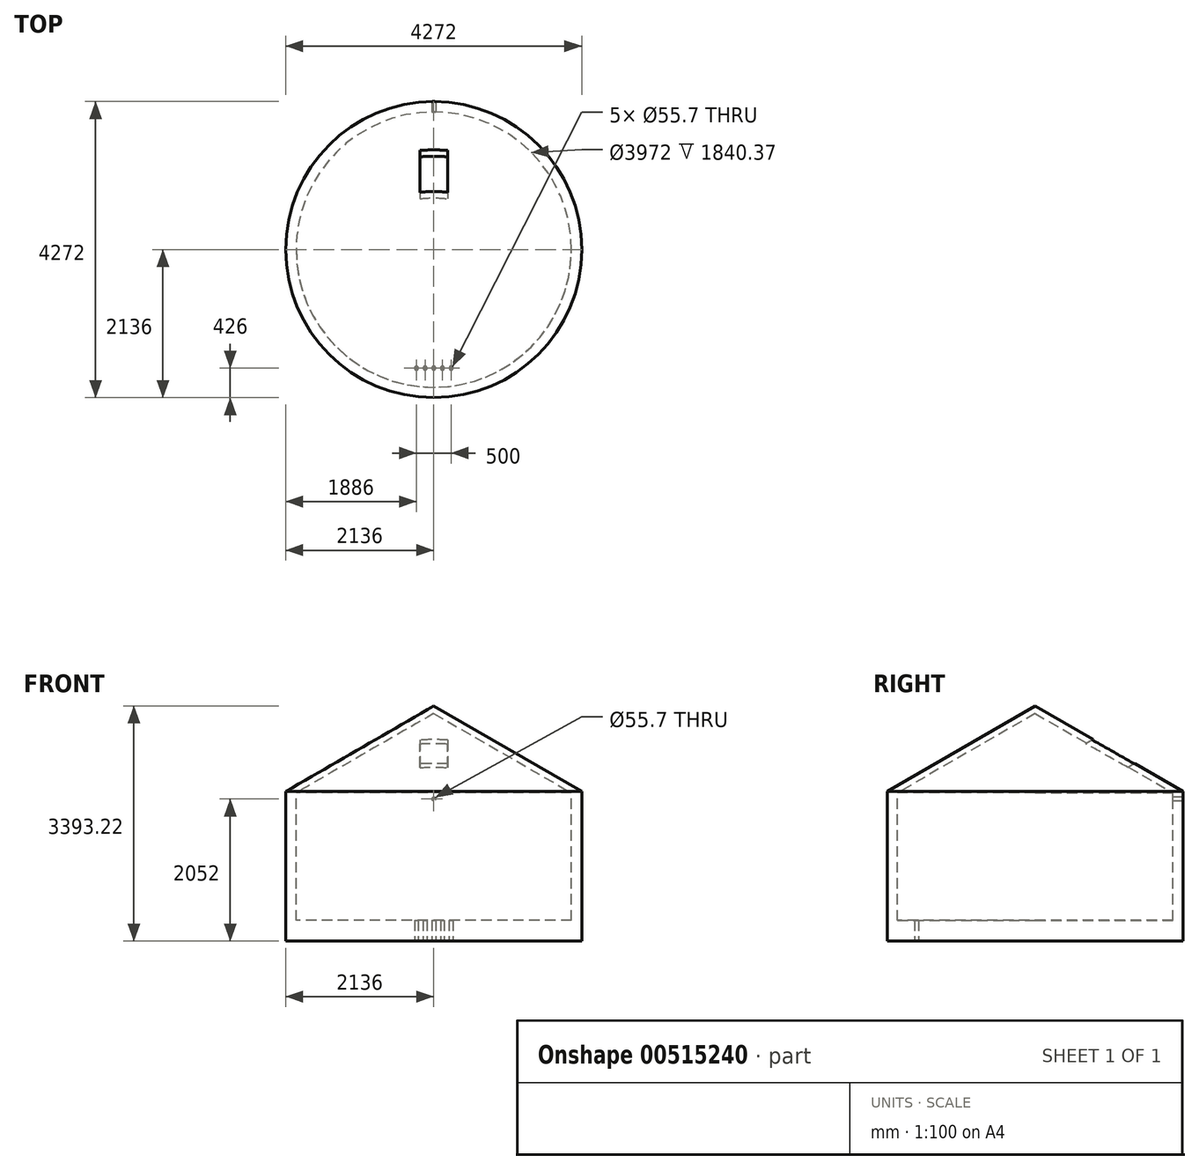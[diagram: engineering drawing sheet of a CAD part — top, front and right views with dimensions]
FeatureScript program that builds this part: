
annotation { "Feature Type Name" : "Feature", "Feature Type Description" : "" }
export const myFeature = defineFeature(function(context is Context, id is Id, definition is map)
    precondition{}
    {
        {
            var Q0;
            Q0=qCreatedBy(makeId("Front.planeOp"),FACE);
            var sketch = newSketch(context, id + "F0", { "sketchPlane" : qUnion([Q0])});
            skLineSegment(sketch, "E0", {"start": v(0, 0) * mm, "end": v(2136, 0) * mm});
            skLineSegment(sketch, "E1", {"start": v(2136, 0) * mm, "end": v(2136, 2160) * mm});
            skLineSegment(sketch, "E2", {"start": v(2136, 2160) * mm, "end": v(0, 3393.22) * mm});
            skLineSegment(sketch, "E3", {"start": v(0, 3393.22) * mm, "end": v(0, 3286.99) * mm});
            skLineSegment(sketch, "E4", {"start": v(0, 3286.99) * mm, "end": v(1986, 2140.37) * mm});
            skLineSegment(sketch, "E5", {"start": v(1986, 2140.37) * mm, "end": v(1986, 300) * mm});
            skLineSegment(sketch, "E6", {"start": v(1986, 300) * mm, "end": v(0, 300) * mm});
            skLineSegment(sketch, "E7", {"start": v(0, 300) * mm, "end": v(0, 0) * mm});
            skSolve(sketch);
        }
        {
            var Q0;
            Q0=sQuery(id+"F0.wireOp",EDGE,"E0");
            cPlane(context, id + "F1", {"entities" : qUnion([Q0]), "cplaneType" : CPlaneType.LINE_ANGLE, "offset" : 25 * mm, "angle" : 30 * degree, "width" : 150 * mm, "height" : 150 * mm});
        }
        {
            var Q0;
            Q0=qCreatedBy(id+"F1.planeOp",FACE);
            var sketch = newSketch(context, id + "F2", { "sketchPlane" : qUnion([Q0])});
            skLineSegment(sketch, "E8.bottom", {"start": v(-200, 2100) * mm, "end": v(200, 2100) * mm});
            skLineSegment(sketch, "E8.top", {"start": v(-200, 1500) * mm, "end": v(200, 1500) * mm});
            skLineSegment(sketch, "E8.left", {"start": v(-200, 2100) * mm, "end": v(-200, 1500) * mm});
            skLineSegment(sketch, "E9.MirrorCS", {"start": v(200, 2100) * mm, "end": v(200, 1500) * mm});
            skSolve(sketch);
        }
        {
            var Q0;
            Q0=qCreatedBy(makeId("Top.planeOp"),FACE);
            var sketch = newSketch(context, id + "F3", { "sketchPlane" : qUnion([Q0])});
            skLineSegment(sketch, "E10", {"start": v(282.73, -1710) * mm, "end": v(-1173.43, -1710) * mm, "construction": true});
            skCircle(sketch, "E11", {"center": v(125, -1710) * mm, "radius": 27.85 * mm});
            skCircle(sketch, "E12", {"center": v(-250, -1710) * mm, "radius": 27.85 * mm});
            skCircle(sketch, "E13", {"center": v(-125, -1710) * mm, "radius": 27.85 * mm});
            skCircle(sketch, "E14", {"center": v(0, -1710) * mm, "radius": 27.85 * mm});
            skCircle(sketch, "E15", {"center": v(250, -1710) * mm, "radius": 27.85 * mm});
            skSolve(sketch);
        }
        {
            var Q0;
            Q0=makeQuery(id+"F0.imprint","IMPRINT",FACE,{"disambiguationData":[TD([[makeQuery(id+"F0.imprint","IMPRINT",EDGE,{"derivedFrom":sQuery(id+"F0.wireOp",EDGE,"E0")}),1.0]])]});
            var Q1;
            Q1=sQuery(id+"F0.wireOp",EDGE,"E7");
            revolve(context, id + "F4", {"entities" : qUnion([Q0]), "axis" : qUnion([Q1]), "revolveType" : RevolveType.FULL});
        }
        {
            var Q0;
            Q0=makeQuery(id+"F2.imprint","IMPRINT",FACE,{"disambiguationData":[TD([[makeQuery(id+"F2.imprint","IMPRINT",EDGE,{"derivedFrom":sQuery(id+"F2.wireOp",EDGE,"E8.bottom")}),-1.0]])]});
            extrude(context, id + "F5", {"entities" : qUnion([Q0]), "operationType" : NewBodyOperationType.REMOVE, "depth" : 30000 * mm, "offsetDistance" : 25 * mm});
        }
        {
            var Q0;
            Q0=makeQuery(id+"F3.imprint","IMPRINT",FACE,{"disambiguationData":[TD([[makeQuery(id+"F3.imprint","IMPRINT",EDGE,{"derivedFrom":sQuery(id+"F3.wireOp",EDGE,"E11")}),1.0]])]});
            var Q1;
            Q1=makeQuery(id+"F3.imprint","IMPRINT",FACE,{"disambiguationData":[TD([[makeQuery(id+"F3.imprint","IMPRINT",EDGE,{"derivedFrom":sQuery(id+"F3.wireOp",EDGE,"E14")}),1.0]])]});
            var Q2;
            Q2=makeQuery(id+"F3.imprint","IMPRINT",FACE,{"disambiguationData":[TD([[makeQuery(id+"F3.imprint","IMPRINT",EDGE,{"derivedFrom":sQuery(id+"F3.wireOp",EDGE,"E13")}),1.0]])]});
            var Q3;
            Q3=makeQuery(id+"F3.imprint","IMPRINT",FACE,{"disambiguationData":[TD([[makeQuery(id+"F3.imprint","IMPRINT",EDGE,{"derivedFrom":sQuery(id+"F3.wireOp",EDGE,"E12")}),1.0]])]});
            var Q4;
            Q4=makeQuery(id+"F3.imprint","IMPRINT",FACE,{"disambiguationData":[TD([[makeQuery(id+"F3.imprint","IMPRINT",EDGE,{"derivedFrom":sQuery(id+"F3.wireOp",EDGE,"E15")}),1.0]])]});
            extrude(context, id + "F6", {"entities" : qUnion([Q0, Q1, Q2, Q3, Q4]), "operationType" : NewBodyOperationType.REMOVE, "depth" : 500 * mm, "offsetDistance" : 25 * mm});
        }
        {
            var Q0;
            Q0=qCreatedBy(makeId("Front.planeOp"),FACE);
            var sketch = newSketch(context, id + "F7", { "sketchPlane" : qUnion([Q0])});
            skCircle(sketch, "E16", {"center": v(0, 2052) * mm, "radius": 27.85 * mm});
            skSolve(sketch);
        }
        {
            var Q0;
            Q0 = qSketchRegion(id + "F7", true);
            extrude(context, id + "F8", {"entities" : qUnion([Q0]), "operationType" : NewBodyOperationType.REMOVE, "endBound" : BoundingType.THROUGH_ALL, "oppositeDirection" : true, "depth" : 25 * mm, "offsetDistance" : 25 * mm});
        }
    });
